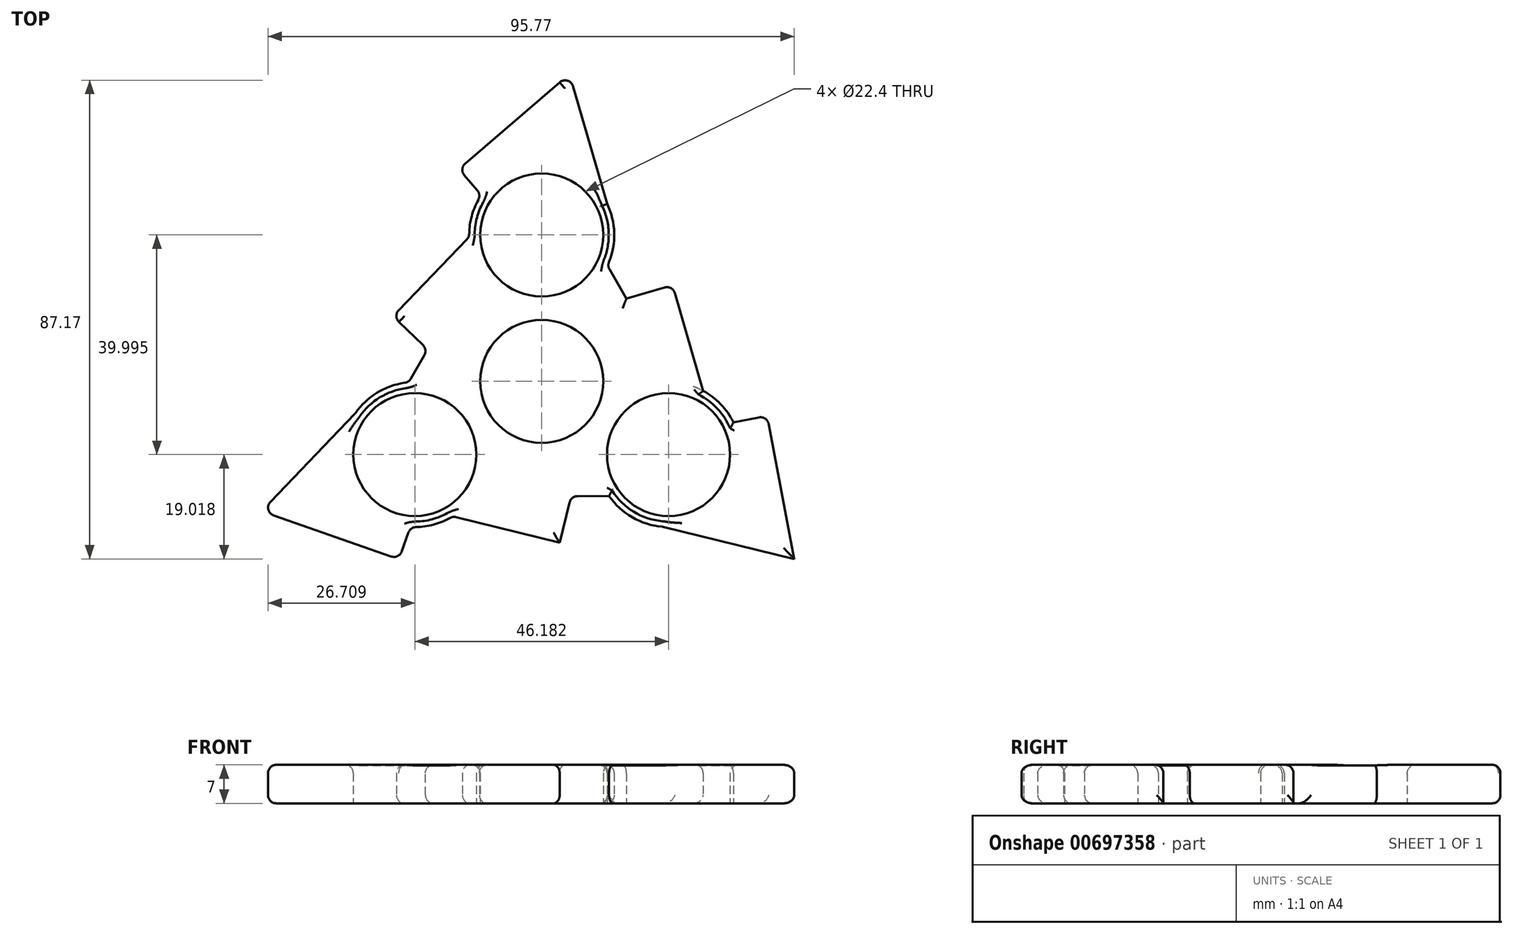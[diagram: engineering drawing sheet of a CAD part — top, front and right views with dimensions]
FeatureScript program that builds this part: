
annotation { "Feature Type Name" : "Feature", "Feature Type Description" : "" }
export const myFeature = defineFeature(function(context is Context, id is Id, definition is map)
    precondition{}
    {
        {
            var Q0;
            Q0=qCreatedBy(makeId("Top.planeOp"),FACE);
            var sketch = newSketch(context, id + "F0", { "sketchPlane" : qUnion([Q0])});
            skCircle(sketch, "E0", {"center": v(0, 0) * mm, "radius": 11.2 * mm});
            skArc(sketch, "E1", {"start": v(-12.2, 5.02) * mm, "mid": v(-12.46, 4.37) * mm, "end": v(-12.67, 3.71) * mm});
            skCircle(sketch, "E2", {"center": v(0, 26.66) * mm, "radius": 11.2 * mm});
            skArc(sketch, "E3", {"start": v(-11, 33.95) * mm, "mid": v(-13.18, 27.4) * mm, "end": v(-11.75, 20.65) * mm});
            skLineSegment(sketch, "E4", {"start": v(5.03, 55.98) * mm, "end": v(-15.07, 38.67) * mm});
            skLineSegment(sketch, "E5", {"start": v(-15.07, 38.67) * mm, "end": v(-11, 33.95) * mm});
            skLineSegment(sketch, "E6", {"start": v(-11.75, 20.65) * mm, "end": v(-15.07, 11.03) * mm});
            skLineSegment(sketch, "E7", {"start": v(-15.07, 11.03) * mm, "end": v(-12.2, 5.02) * mm});
            skLineSegment(sketch, "E8", {"start": v(5.03, 55.98) * mm, "end": v(11.92, 32.33) * mm});
            skLineSegment(sketch, "E9", {"start": v(11.95, 21.06) * mm, "end": v(9.55, 9.11) * mm});
            skArc(sketch, "E10.1.0", {"start": v(-24.21, -0.18) * mm, "mid": v(-29.72, -1.92) * mm, "end": v(-33.96, -5.84) * mm});
            skCircle(sketch, "E10.1.1", {"center": v(-23.1, -13.33) * mm, "radius": 11.2 * mm});
            skLineSegment(sketch, "E10.1.2", {"start": v(-51, -23.63) * mm, "end": v(-33.96, -5.84) * mm});
            skLineSegment(sketch, "E10.1.3", {"start": v(-51, -23.63) * mm, "end": v(-25.95, -32.39) * mm});
            skLineSegment(sketch, "E10.1.4", {"start": v(-25.95, -32.39) * mm, "end": v(-23.9, -26.5) * mm});
            skLineSegment(sketch, "E10.1.5", {"start": v(-12, -20.5) * mm, "end": v(-2.01, -18.56) * mm});
            skLineSegment(sketch, "E10.1.6", {"start": v(-2.01, -18.56) * mm, "end": v(1.76, -13.08) * mm});
            skLineSegment(sketch, "E10.1.7", {"start": v(-24.21, -0.18) * mm, "end": v(-12.67, 3.71) * mm});
            skArc(sketch, "E10.2.0", {"start": v(12.26, -20.88) * mm, "mid": v(16.52, -24.78) * mm, "end": v(22.04, -26.49) * mm});
            skCircle(sketch, "E10.2.1", {"center": v(23.1, -13.33) * mm, "radius": 11.2 * mm});
            skLineSegment(sketch, "E10.2.2", {"start": v(45.97, -32.35) * mm, "end": v(22.04, -26.49) * mm});
            skLineSegment(sketch, "E10.2.3", {"start": v(45.97, -32.35) * mm, "end": v(41.02, -6.28) * mm});
            skLineSegment(sketch, "E10.2.4", {"start": v(41.02, -6.28) * mm, "end": v(34.9, -7.44) * mm});
            skLineSegment(sketch, "E10.2.5", {"start": v(23.76, -0.15) * mm, "end": v(17.08, 7.54) * mm});
            skLineSegment(sketch, "E10.2.6", {"start": v(17.08, 7.54) * mm, "end": v(10.45, 8.06) * mm});
            skLineSegment(sketch, "E10.2.7", {"start": v(12.26, -20.88) * mm, "end": v(3.12, -12.83) * mm});
            skLineSegment(sketch, "E11", {"start": v(-13.2, 26.3) * mm, "end": v(-27.08, 11.86) * mm});
            skLineSegment(sketch, "E12", {"start": v(-27.08, 11.86) * mm, "end": v(-20.79, 5.82) * mm});
            skLineSegment(sketch, "E13", {"start": v(-20.79, 5.82) * mm, "end": v(-24.21, -0.18) * mm});
            skLineSegment(sketch, "E14.1.0", {"start": v(3.26, -29.38) * mm, "end": v(5.35, -20.91) * mm});
            skLineSegment(sketch, "E14.1.1", {"start": v(-16.19, -24.58) * mm, "end": v(3.26, -29.38) * mm});
            skLineSegment(sketch, "E14.1.2", {"start": v(5.35, -20.91) * mm, "end": v(12.26, -20.88) * mm});
            skLineSegment(sketch, "E14.2.0", {"start": v(23.81, 17.52) * mm, "end": v(15.43, 15.1) * mm});
            skLineSegment(sketch, "E14.2.1", {"start": v(29.38, -1.73) * mm, "end": v(23.81, 17.52) * mm});
            skLineSegment(sketch, "E14.2.2", {"start": v(15.43, 15.1) * mm, "end": v(11.95, 21.06) * mm});
            skArc(sketch, "E15.trimOffspring", {"start": v(11.95, 21.06) * mm, "mid": v(13.2, 26.7) * mm, "end": v(11.92, 32.33) * mm});
            skArc(sketch, "E16.trimOffspring", {"start": v(1.76, -13.08) * mm, "mid": v(2.44, -12.97) * mm, "end": v(3.12, -12.83) * mm});
            skArc(sketch, "E17.trimOffspring", {"start": v(10.45, 8.06) * mm, "mid": v(10.01, 8.6) * mm, "end": v(9.55, 9.11) * mm});
            skArc(sketch, "E18.trimOffspring", {"start": v(34.9, -7.44) * mm, "mid": v(30.32, -2.29) * mm, "end": v(23.76, -0.15) * mm});
            skArc(sketch, "E19.trimOffspring", {"start": v(-23.9, -26.5) * mm, "mid": v(-17.14, -25.11) * mm, "end": v(-12, -20.5) * mm});
            skSolve(sketch);
        }
        {
            var Q0;
            Q0=makeQuery(id+"F0.imprint","IMPRINT",FACE,{"disambiguationData":[TD([[makeQuery(id+"F0.imprint","IMPRINT",EDGE,{"derivedFrom":sQuery(id+"F0.wireOp",EDGE,"E0")}),-1.0]])]});
            var Q1;
            Q1=makeQuery(id+"F0.imprint","IMPRINT",FACE,{"disambiguationData":[TD([[makeQuery(id+"F0.imprint","IMPRINT",EDGE,{"derivedFrom":sQuery(id+"F0.wireOp",EDGE,"E1")}),-1.0]])]});
            var Q2;
            Q2=makeQuery(id+"F0.imprint","IMPRINT",FACE,{"disambiguationData":[TD([[makeQuery(id+"F0.imprint","IMPRINT",EDGE,{"derivedFrom":sQuery(id+"F0.wireOp",EDGE,"E9")}),1.0]])]});
            var Q3;
            {var subQ0=sQuery(id+"F0.wireOp",EDGE,"E10.1.5");Q3=makeQuery(id+"F0.imprint","IMPRINT",FACE,{"disambiguationData":[TD([[makeQuery(id+"F0.imprint","IMPRINT",EDGE,{"derivedFrom":subQ0}),-1.0]])]});}
            extrude(context, id + "F1", {"entities" : qUnion([Q0, Q1, Q2, Q3]), "depth" : 7 * mm, "offsetDistance" : 25 * mm});
        }
        {
            var Q0;
            Q0=makeQuery(id+"F1.opExtrude","CAP_EDGE",EDGE,{"disambiguationData":[OSD([sQuery(id+"F0.wireOp",EDGE,"E10.2.3")])],"isStart":false});
            var Q1;
            Q1=makeQuery(id+"F1.opExtrude","CAP_EDGE",EDGE,{"disambiguationData":[OSD([sQuery(id+"F0.wireOp",EDGE,"E18.trimOffspring")])],"isStart":false});
            var Q2;
            Q2=makeQuery(id+"F1.opExtrude","CAP_EDGE",EDGE,{"disambiguationData":[OSD([sQuery(id+"F0.wireOp",EDGE,"E14.2.1")])],"isStart":false});
            var Q3;
            Q3=makeQuery(id+"F1.opExtrude","CAP_EDGE",EDGE,{"disambiguationData":[OSD([sQuery(id+"F0.wireOp",EDGE,"E14.2.0")])],"isStart":false});
            var Q4;
            Q4=makeQuery(id+"F1.opExtrude","CAP_FACE",FACE,{"disambiguationData":[OSD([sQuery(id+"F0.wireOp",EDGE,"E0"),sQuery(id+"F0.wireOp",EDGE,"E2"),sQuery(id+"F0.wireOp",EDGE,"E3"),sQuery(id+"F0.wireOp",EDGE,"E4"),sQuery(id+"F0.wireOp",EDGE,"E5"),sQuery(id+"F0.wireOp",EDGE,"E8"),sQuery(id+"F0.wireOp",EDGE,"E10.1.0"),sQuery(id+"F0.wireOp",EDGE,"E10.1.1"),sQuery(id+"F0.wireOp",EDGE,"E10.1.2"),sQuery(id+"F0.wireOp",EDGE,"E10.1.3"),sQuery(id+"F0.wireOp",EDGE,"E10.1.4"),sQuery(id+"F0.wireOp",EDGE,"E10.2.0"),sQuery(id+"F0.wireOp",EDGE,"E10.2.1"),sQuery(id+"F0.wireOp",EDGE,"E10.2.2"),sQuery(id+"F0.wireOp",EDGE,"E10.2.3"),sQuery(id+"F0.wireOp",EDGE,"E10.2.4"),sQuery(id+"F0.wireOp",EDGE,"E11"),sQuery(id+"F0.wireOp",EDGE,"E12"),sQuery(id+"F0.wireOp",EDGE,"E13"),sQuery(id+"F0.wireOp",EDGE,"E14.1.0"),sQuery(id+"F0.wireOp",EDGE,"E14.1.1"),sQuery(id+"F0.wireOp",EDGE,"E14.1.2"),sQuery(id+"F0.wireOp",EDGE,"E14.2.0"),sQuery(id+"F0.wireOp",EDGE,"E14.2.1"),sQuery(id+"F0.wireOp",EDGE,"E14.2.2"),sQuery(id+"F0.wireOp",EDGE,"E15.trimOffspring"),sQuery(id+"F0.wireOp",EDGE,"E18.trimOffspring"),sQuery(id+"F0.wireOp",EDGE,"E19.trimOffspring")])],"isStart":false});
            var Q5;
            Q5=makeQuery(id+"F1.opExtrude","CAP_EDGE",EDGE,{"disambiguationData":[OSD([sQuery(id+"F0.wireOp",EDGE,"E3")])],"isStart":true});
            var Q6;
            Q6=makeQuery(id+"F1.opExtrude","CAP_EDGE",EDGE,{"disambiguationData":[OSD([sQuery(id+"F0.wireOp",EDGE,"E5")])],"isStart":true});
            var Q7;
            Q7=makeQuery(id+"F1.opExtrude","CAP_EDGE",EDGE,{"disambiguationData":[OSD([sQuery(id+"F0.wireOp",EDGE,"E4")])],"isStart":true});
            var Q8;
            Q8=makeQuery(id+"F1.opExtrude","CAP_EDGE",EDGE,{"disambiguationData":[OSD([sQuery(id+"F0.wireOp",EDGE,"E11")])],"isStart":true});
            var Q9;
            Q9=makeQuery(id+"F1.opExtrude","CAP_EDGE",EDGE,{"disambiguationData":[OSD([sQuery(id+"F0.wireOp",EDGE,"E12")])],"isStart":true});
            var Q10;
            Q10=makeQuery(id+"F1.opExtrude","CAP_EDGE",EDGE,{"disambiguationData":[OSD([sQuery(id+"F0.wireOp",EDGE,"E10.1.2")])],"isStart":true});
            var Q11;
            Q11=makeQuery(id+"F1.opExtrude","CAP_EDGE",EDGE,{"disambiguationData":[OSD([sQuery(id+"F0.wireOp",EDGE,"E10.1.0")])],"isStart":true});
            var Q12;
            Q12=makeQuery(id+"F1.opExtrude","CAP_EDGE",EDGE,{"disambiguationData":[OSD([sQuery(id+"F0.wireOp",EDGE,"E10.1.3")])],"isStart":true});
            var Q13;
            Q13=makeQuery(id+"F1.opExtrude","SWEPT_EDGE",EDGE,{"disambiguationData":[OSD([sQuery(id+"F0.wireOp",EDGE,"E10.1.3"),sQuery(id+"F0.wireOp",EDGE,"E10.1.4")])]});
            var Q14;
            Q14=makeQuery(id+"F1.opExtrude","SWEPT_EDGE",EDGE,{"disambiguationData":[OSD([sQuery(id+"F0.wireOp",EDGE,"E10.1.2"),sQuery(id+"F0.wireOp",EDGE,"E10.1.3")])]});
            var Q15;
            Q15=makeQuery(id+"F1.opExtrude","SWEPT_EDGE",EDGE,{"disambiguationData":[OSD([sQuery(id+"F0.wireOp",EDGE,"E10.1.0"),sQuery(id+"F0.wireOp",EDGE,"E10.1.2")])]});
            var Q16;
            Q16=makeQuery(id+"F1.opExtrude","SWEPT_FACE",FACE,{"disambiguationData":[OSD([sQuery(id+"F0.wireOp",EDGE,"E13")])]});
            var Q17;
            Q17=makeQuery(id+"F1.opExtrude","SWEPT_FACE",FACE,{"disambiguationData":[OSD([sQuery(id+"F0.wireOp",EDGE,"E3")])]});
            var Q18;
            Q18=makeQuery(id+"F1.opExtrude","SWEPT_EDGE",EDGE,{"disambiguationData":[OSD([sQuery(id+"F0.wireOp",EDGE,"E4"),sQuery(id+"F0.wireOp",EDGE,"E5")])]});
            var Q19;
            Q19=makeQuery(id+"F1.opExtrude","SWEPT_EDGE",EDGE,{"disambiguationData":[OSD([sQuery(id+"F0.wireOp",EDGE,"E4"),sQuery(id+"F0.wireOp",EDGE,"E8")])]});
            var Q20;
            Q20=makeQuery(id+"F1.opExtrude","CAP_EDGE",EDGE,{"disambiguationData":[OSD([sQuery(id+"F0.wireOp",EDGE,"E14.2.1")])],"isStart":true});
            var Q21;
            Q21=makeQuery(id+"F1.opExtrude","CAP_EDGE",EDGE,{"disambiguationData":[OSD([sQuery(id+"F0.wireOp",EDGE,"E15.trimOffspring")])],"isStart":true});
            var Q22;
            Q22=makeQuery(id+"F1.opExtrude","CAP_EDGE",EDGE,{"disambiguationData":[OSD([sQuery(id+"F0.wireOp",EDGE,"E8")])],"isStart":true});
            var Q23;
            Q23=makeQuery(id+"F1.opExtrude","CAP_EDGE",EDGE,{"disambiguationData":[OSD([sQuery(id+"F0.wireOp",EDGE,"E10.2.2")])],"isStart":true});
            var Q24;
            Q24=makeQuery(id+"F1.opExtrude","CAP_EDGE",EDGE,{"disambiguationData":[OSD([sQuery(id+"F0.wireOp",EDGE,"E10.2.3")])],"isStart":true});
            var Q25;
            Q25=makeQuery(id+"F1.opExtrude","SWEPT_EDGE",EDGE,{"disambiguationData":[OSD([sQuery(id+"F0.wireOp",EDGE,"E10.2.3"),sQuery(id+"F0.wireOp",EDGE,"E10.2.4")])]});
            var Q26;
            Q26=makeQuery(id+"F1.opExtrude","CAP_EDGE",EDGE,{"disambiguationData":[OSD([sQuery(id+"F0.wireOp",EDGE,"E14.1.0")])],"isStart":true});
            var Q27;
            Q27=makeQuery(id+"F1.opExtrude","CAP_EDGE",EDGE,{"disambiguationData":[OSD([sQuery(id+"F0.wireOp",EDGE,"E10.2.0")])],"isStart":true});
            var Q28;
            Q28=makeQuery(id+"F1.opExtrude","CAP_EDGE",EDGE,{"disambiguationData":[OSD([sQuery(id+"F0.wireOp",EDGE,"E14.1.2")])],"isStart":true});
            var Q29;
            Q29=makeQuery(id+"F1.opExtrude","CAP_EDGE",EDGE,{"disambiguationData":[OSD([sQuery(id+"F0.wireOp",EDGE,"E14.1.1")])],"isStart":true});
            var Q30;
            Q30=makeQuery(id+"F1.opExtrude","CAP_EDGE",EDGE,{"disambiguationData":[OSD([sQuery(id+"F0.wireOp",EDGE,"E19.trimOffspring")])],"isStart":true});
            var Q31;
            Q31=makeQuery(id+"F1.opExtrude","CAP_EDGE",EDGE,{"disambiguationData":[OSD([sQuery(id+"F0.wireOp",EDGE,"E10.1.4")])],"isStart":true});
            var Q32;
            Q32=makeQuery(id+"F1.opExtrude","SWEPT_EDGE",EDGE,{"disambiguationData":[OSD([sQuery(id+"F0.wireOp",EDGE,"E14.1.0"),sQuery(id+"F0.wireOp",EDGE,"E14.1.2")])]});
            var Q33;
            Q33=makeQuery(id+"F1.opExtrude","SWEPT_EDGE",EDGE,{"disambiguationData":[OSD([sQuery(id+"F0.wireOp",EDGE,"E14.1.1"),sQuery(id+"F0.wireOp",EDGE,"E19.trimOffspring")])]});
            var Q34;
            Q34=makeQuery(id+"F1.opExtrude","CAP_EDGE",EDGE,{"disambiguationData":[OSD([sQuery(id+"F0.wireOp",EDGE,"E15.trimOffspring")])],"isStart":false});
            var Q35;
            Q35=makeQuery(id+"F1.opExtrude","SWEPT_EDGE",EDGE,{"disambiguationData":[OSD([sQuery(id+"F0.wireOp",EDGE,"E9"),sQuery(id+"F0.wireOp",EDGE,"E14.2.2"),sQuery(id+"F0.wireOp",EDGE,"E15.trimOffspring")])]});
            var Q36;
            Q36=makeQuery(id+"F1.opExtrude","CAP_EDGE",EDGE,{"disambiguationData":[OSD([sQuery(id+"F0.wireOp",EDGE,"E14.2.2")])],"isStart":false});
            var Q37;
            Q37=makeQuery(id+"F1.opExtrude","SWEPT_EDGE",EDGE,{"disambiguationData":[OSD([sQuery(id+"F0.wireOp",EDGE,"E14.2.0"),sQuery(id+"F0.wireOp",EDGE,"E14.2.1")])]});
            var Q38;
            Q38=makeQuery(id+"F1.opExtrude","CAP_EDGE",EDGE,{"disambiguationData":[OSD([sQuery(id+"F0.wireOp",EDGE,"E8")])],"isStart":false});
            var Q39;
            Q39=makeQuery(id+"F1.opExtrude","CAP_EDGE",EDGE,{"disambiguationData":[OSD([sQuery(id+"F0.wireOp",EDGE,"E10.2.2")])],"isStart":false});
            var Q40;
            Q40=makeQuery(id+"F1.opExtrude","SWEPT_EDGE",EDGE,{"disambiguationData":[OSD([sQuery(id+"F0.wireOp",EDGE,"E10.2.0"),sQuery(id+"F0.wireOp",EDGE,"E10.2.2")])]});
            var Q41;
            Q41=makeQuery(id+"F1.opExtrude","SWEPT_EDGE",EDGE,{"disambiguationData":[OSD([sQuery(id+"F0.wireOp",EDGE,"E10.1.4"),sQuery(id+"F0.wireOp",EDGE,"E19.trimOffspring")])]});
            var Q42;
            Q42=makeQuery(id+"F1.opExtrude","SWEPT_EDGE",EDGE,{"disambiguationData":[OSD([sQuery(id+"F0.wireOp",EDGE,"E11"),sQuery(id+"F0.wireOp",EDGE,"E12")])]});
            var Q43;
            Q43=makeQuery(id+"F1.opExtrude","CAP_EDGE",EDGE,{"disambiguationData":[OSD([sQuery(id+"F0.wireOp",EDGE,"E13")])],"isStart":true});
            fillet(context, id + "F2", {"entities" : qUnion([Q0, Q1, Q2, Q3, Q4, Q5, Q6, Q7, Q8, Q9, Q10, Q11, Q12, Q13, Q14, Q15, Q16, Q17, Q18, Q19, Q20, Q21, Q22, Q23, Q24, Q25, Q26, Q27, Q28, Q29, Q30, Q31, Q32, Q33, Q34, Q35, Q36, Q37, Q38, Q39, Q40, Q41, Q42, Q43]), "radius" : 1.5 * mm, "tangentPropagation" : true, "allowEdgeOverflow" : false});
        }
    });
